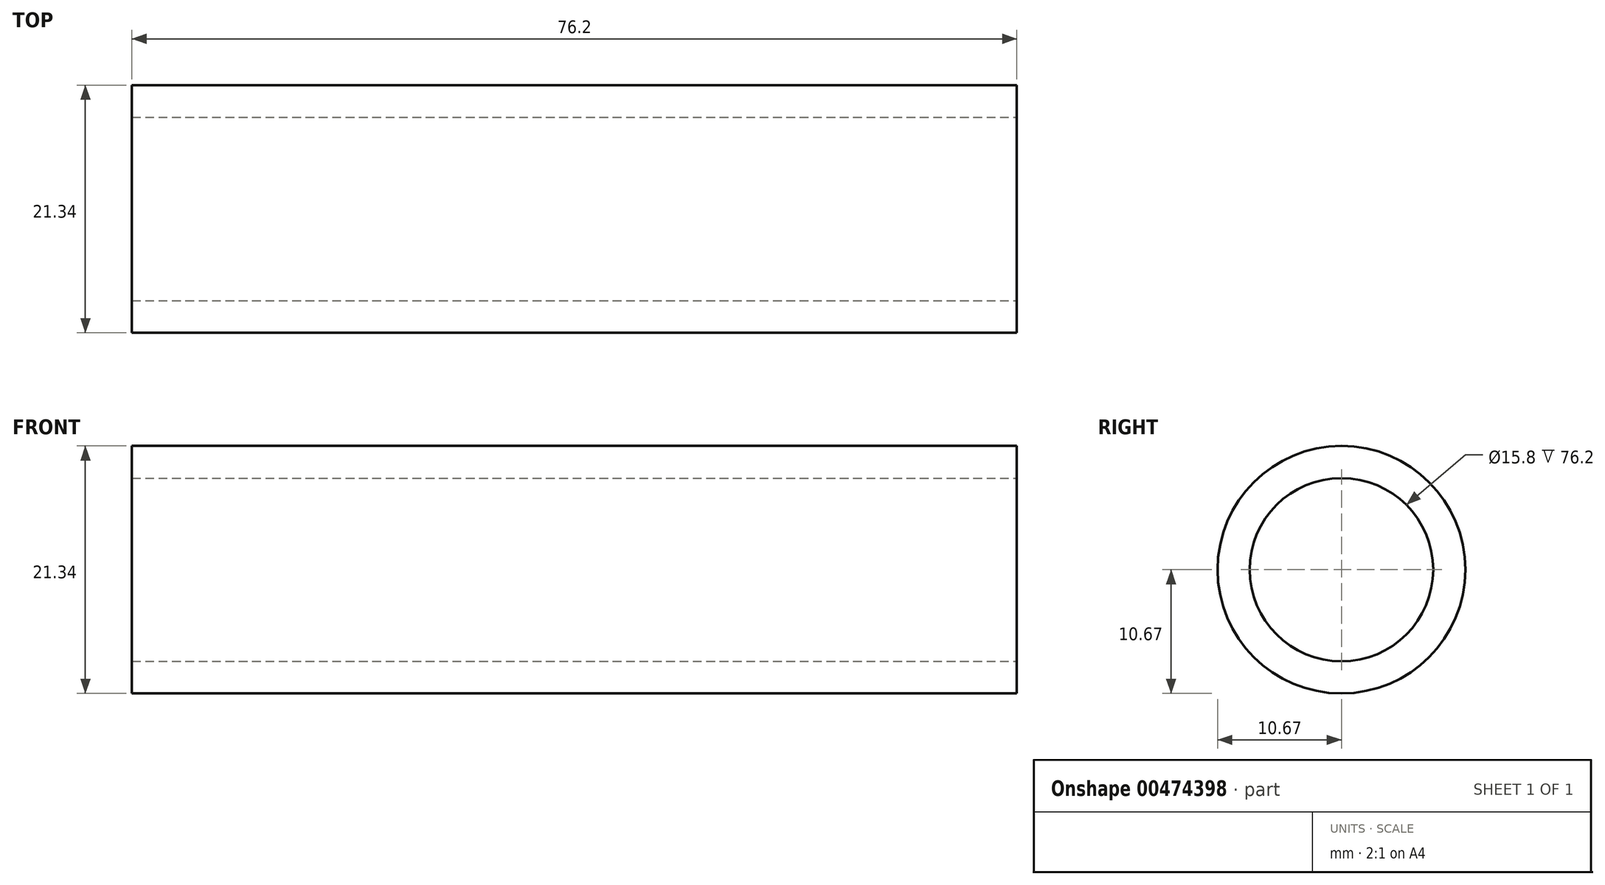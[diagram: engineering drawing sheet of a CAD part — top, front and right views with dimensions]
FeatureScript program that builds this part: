
annotation { "Feature Type Name" : "Feature", "Feature Type Description" : "" }
export const myFeature = defineFeature(function(context is Context, id is Id, definition is map)
    precondition{}
    {
        {
            var Q0;
            Q0=qCreatedBy(makeId("Front.planeOp"),FACE);
            var sketch = newSketch(context, id + "F0", { "sketchPlane" : qUnion([Q0])});
            skLineSegment(sketch, "E0.bottom", {"start": v(0, 0) * mm, "end": v(76.2, 0) * mm});
            skLineSegment(sketch, "E0.top", {"start": v(0, 10.67) * mm, "end": v(76.2, 10.67) * mm});
            skLineSegment(sketch, "E0.left", {"start": v(0, 0) * mm, "end": v(0, 10.67) * mm});
            skLineSegment(sketch, "E0.right", {"start": v(76.2, 0) * mm, "end": v(76.2, 10.67) * mm});
            skLineSegment(sketch, "E1.bottom", {"start": v(76.2, 0) * mm, "end": v(76.2, 0) * mm});
            skLineSegment(sketch, "E1.top", {"start": v(76.2, 10.67) * mm, "end": v(76.2, 10.67) * mm});
            skSolve(sketch);
        }
        {
            var Q0;
            Q0=makeQuery(id+"F0.imprint","IMPRINT",FACE,{"disambiguationData":[TD([[makeQuery(id+"F0.imprint","IMPRINT",EDGE,{"derivedFrom":sQuery(id+"F0.wireOp",EDGE,"E0.bottom")}),1.0]])]});
            var Q1;
            Q1=makeQuery(id+"F0.imprint","IMPRINT",FACE,{"disambiguationData":[TD([[makeQuery(id+"F0.imprint","IMPRINT",EDGE,{"derivedFrom":sQuery(id+"F0.wireOp",EDGE,"eb63q3lU-USBM-ynMG-UXLy-Mur0R52FMiaT.bottom")}),-1.0]])]});
            var Q2;
            Q2=sQuery(id+"F0.wireOp",EDGE,"E0.bottom");
            revolve(context, id + "F1", {"entities" : qUnion([Q0, Q1]), "axis" : qUnion([Q2]), "revolveType" : RevolveType.FULL});
        }
        {
            var Q0;
            Q0=makeQuery(id+"F1.opRevolve","SWEPT_FACE",FACE,{"disambiguationData":[OSD([sQuery(id+"F0.wireOp",EDGE,"E0.right")])]});
            var sketch = newSketch(context, id + "F2", { "sketchPlane" : qUnion([Q0])});
            skCircle(sketch, "E2", {"center": v(0, 0) * mm, "radius": 7.9 * mm});
            skSolve(sketch);
        }
        {
            var Q0;
            Q0=makeQuery(id+"F2.imprint","IMPRINT",FACE,{"disambiguationData":[TD([[makeQuery(id+"F2.imprint","IMPRINT",EDGE,{"derivedFrom":sQuery(id+"F2.wireOp",EDGE,"E2")}),1.0]])]});
            extrude(context, id + "F3", {"entities" : qUnion([Q0]), "operationType" : NewBodyOperationType.REMOVE, "endBound" : BoundingType.UP_TO_NEXT, "oppositeDirection" : true, "depth" : 25.4 * mm});
        }
    });
